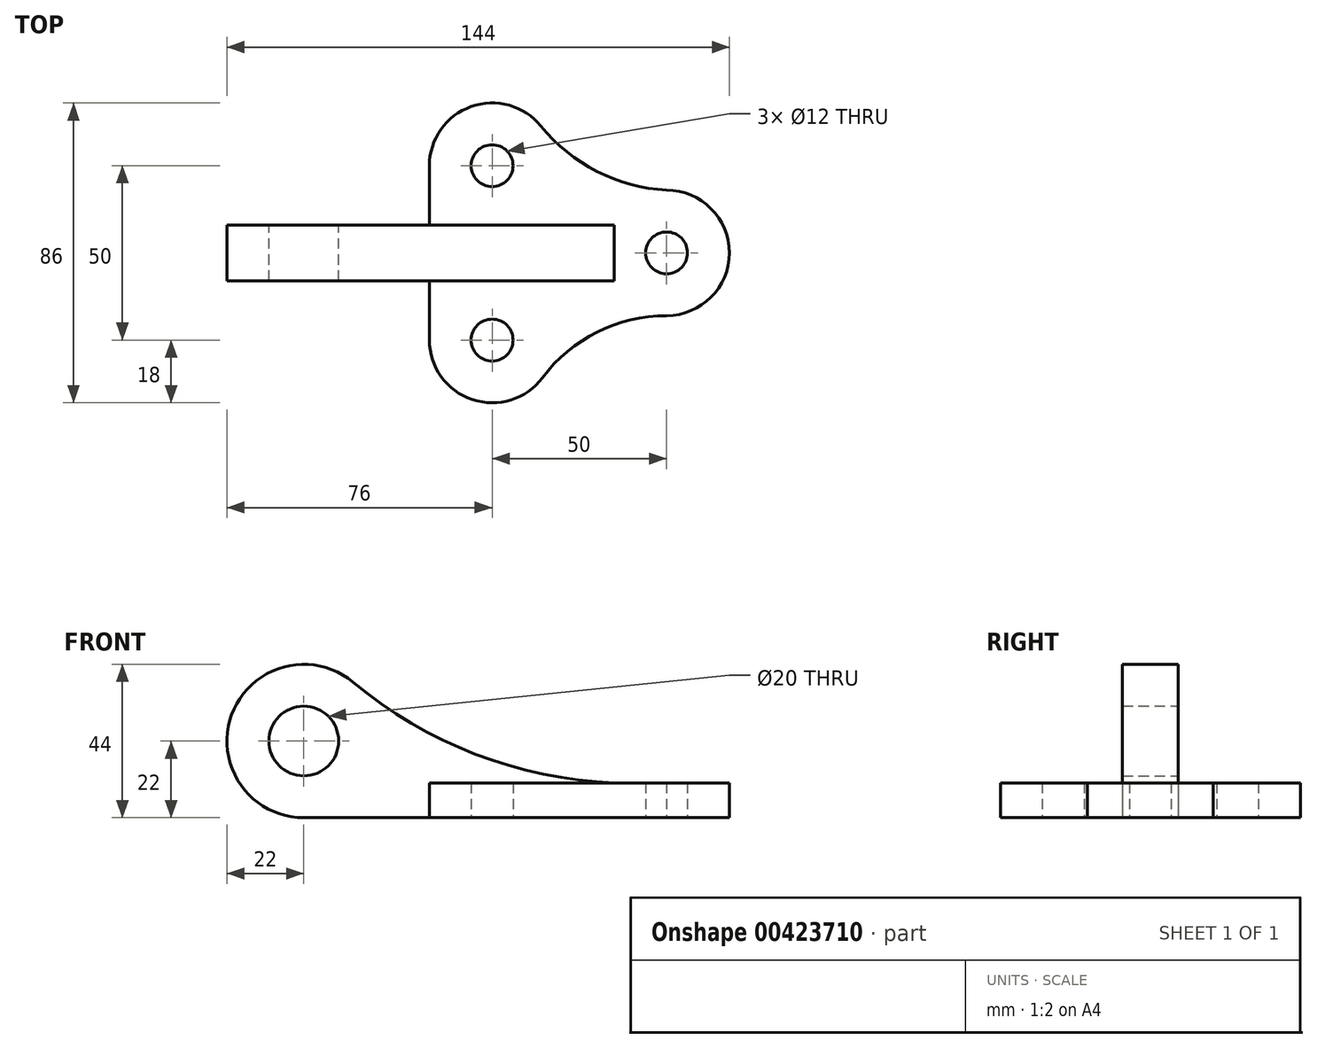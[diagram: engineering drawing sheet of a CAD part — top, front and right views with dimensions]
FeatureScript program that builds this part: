
annotation { "Feature Type Name" : "Feature", "Feature Type Description" : "" }
export const myFeature = defineFeature(function(context is Context, id is Id, definition is map)
    precondition{}
    {
        {
            var Q0;
            Q0=qCreatedBy(makeId("Top.planeOp"),FACE);
            var sketch = newSketch(context, id + "F0", { "sketchPlane" : qUnion([Q0])});
            skArc(sketch, "E0", {"start": v(0, -18) * mm, "mid": v(18, 0) * mm, "end": v(0, 18) * mm});
            skArc(sketch, "E1", {"start": v(-36.04, 36.36) * mm, "mid": v(-56.03, 41.96) * mm, "end": v(-68, 25) * mm});
            skArc(sketch, "E2", {"start": v(-68, -25) * mm, "mid": v(-55.7, -42.08) * mm, "end": v(-35.6, -35.8) * mm});
            skCircle(sketch, "E3", {"center": v(0, 0) * mm, "radius": 6 * mm});
            skCircle(sketch, "E4", {"center": v(-50, 25) * mm, "radius": 6 * mm});
            skCircle(sketch, "E5", {"center": v(-50, -25) * mm, "radius": 6 * mm});
            skLineSegment(sketch, "E6", {"start": v(-68, 25) * mm, "end": v(-68, -25) * mm});
            skArc(sketch, "E7", {"start": v(-36.04, 36.36) * mm, "mid": v(-19.96, 23.37) * mm, "end": v(0, 18) * mm});
            skArc(sketch, "E8", {"start": v(0, -18) * mm, "mid": v(-19.9, -22.7) * mm, "end": v(-35.6, -35.8) * mm});
            skSolve(sketch);
        }
        {
            var Q0;
            Q0=makeQuery(id+"F0.imprint","IMPRINT",FACE,{"disambiguationData":[TD([[makeQuery(id+"F0.imprint","IMPRINT",EDGE,{"derivedFrom":sQuery(id+"F0.wireOp",EDGE,"E0")}),1.0]])]});
            extrude(context, id + "F1", {"entities" : qUnion([Q0]), "depth" : 10 * mm});
        }
        {
            var Q0;
            Q0=qCreatedBy(makeId("Front.planeOp"),FACE);
            var sketch = newSketch(context, id + "F2", { "sketchPlane" : qUnion([Q0])});
            skCircle(sketch, "E9", {"center": v(-104, 22) * mm, "radius": 10 * mm});
            skArc(sketch, "E10", {"start": v(-89.9, 38.9) * mm, "mid": v(-124.68, 29.5) * mm, "end": v(-104, 0) * mm});
            skLineSegment(sketch, "E11.0", {"start": v(-6, 10) * mm, "end": v(6, 10) * mm, "construction": true});
            skLineSegment(sketch, "E12", {"start": v(-104, 0) * mm, "end": v(6, 0) * mm});
            skLineSegment(sketch, "E13.0", {"start": v(0, 10) * mm, "end": v(-35.6, 10) * mm, "construction": true});
            skArc(sketch, "E14", {"start": v(-89.9, 38.9) * mm, "mid": v(-54.84, 18.27) * mm, "end": v(-15, 10) * mm});
            skPoint(sketch, "E15", {"position": v(-17.8, 10) * mm});
            skLineSegment(sketch, "E16", {"start": v(-15, 10) * mm, "end": v(-15, 0) * mm});
            skSolve(sketch);
        }
        {
            var Q0;
            Q0=makeQuery(id+"F2.imprint","IMPRINT",FACE,{"disambiguationData":[TD([[makeQuery(id+"F2.imprint","IMPRINT",EDGE,{"derivedFrom":sQuery(id+"F2.wireOp",EDGE,"E9")}),-1.0]])]});
            extrude(context, id + "F3", {"entities" : qUnion([Q0]), "operationType" : NewBodyOperationType.ADD, "depth" : 8 * mm, "hasSecondDirection" : true, "secondDirectionOppositeDirection" : true, "secondDirectionDepth" : 8 * mm});
        }
    });
